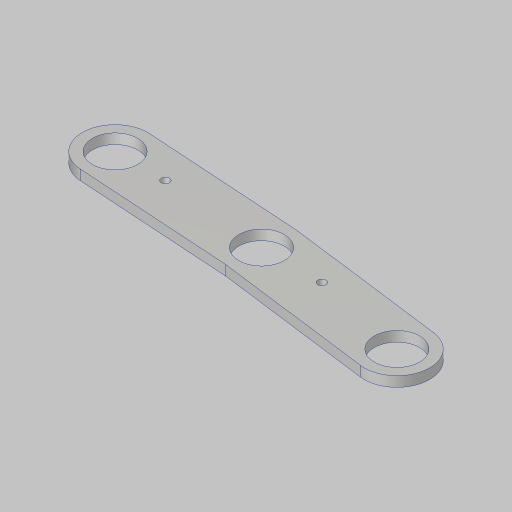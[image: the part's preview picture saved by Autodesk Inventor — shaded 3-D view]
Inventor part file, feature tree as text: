
AUTODESK INVENTOR PART (.ipt)
format: ipt  version: 2023.5 (Build 275446000, 446)  size: 125,440 bytes
history: native  units: in
note: dims shown in document units (in); Inventor stores cm internally (conversion verified against a paired STEP export)
features: sketch x1, extrude x1, hole x1
ambient origin geometry x8: Origin, YZ Plane, XZ Plane, XY Plane, X Axis, Y Axis, Z Axis, Center Point
bodies: Solid1 (feature_tree)
feature tree (3):
  sketch  "Sketch1"  dims[d0=1.125in d1=3.8976in d2=3.8976in d3=0.5in d4=0.25in d5=0.25in d6=0.25in d7=0.25in d8=1.25in d9=1.5in d10=0.375in d11=0.25in d12=0.25in d13=0.0in d14=0.201in d15=0.75in d16=0.385in d17=0.25in d18=0.5635in d19=1.0in d20=0.8108in]
  extrude  "Extrusion1"  Depth=3.8976in
  hole  "Hole1"  [1 undecoded]
note: 1 required parameter value undecoded (feature->parameter linkage not recoverable at this tier; creation-order binding heuristic only, values carry confidence <= 0.55)
